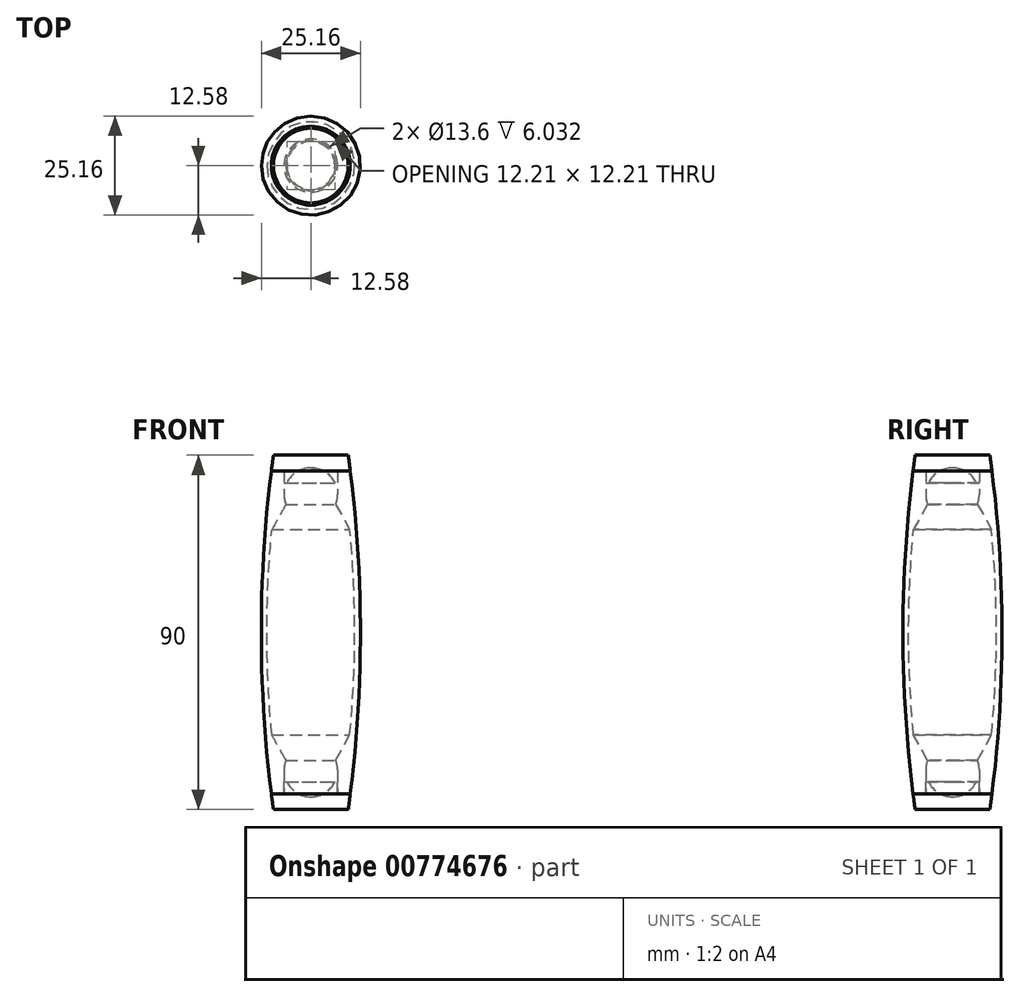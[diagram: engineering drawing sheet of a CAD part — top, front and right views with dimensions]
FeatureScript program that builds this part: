
annotation { "Feature Type Name" : "Feature", "Feature Type Description" : "" }
export const myFeature = defineFeature(function(context is Context, id is Id, definition is map)
    precondition{}
    {
        {
            var Q0;
            Q0=qCreatedBy(makeId("Front.planeOp"),FACE);
            var sketch = newSketch(context, id + "F0", { "sketchPlane" : qUnion([Q0])});
            skPoint(sketch, "E0.middle", {"position": v(0, 0) * mm});
            skLineSegment(sketch, "E1.bottom", {"start": v(0, -45) * mm, "end": v(-12.5, -45) * mm});
            skLineSegment(sketch, "E1.top", {"start": v(0, 45) * mm, "end": v(-12.5, 45) * mm});
            skPoint(sketch, "E2", {"position": v(-9.5, 45) * mm});
            skPoint(sketch, "E3.MirrorP", {"position": v(-9.5, -45) * mm});
            skPoint(sketch, "E4", {"position": v(-12.5, 0) * mm});
            skArc(sketch, "E5", {"start": v(-9.5, 45) * mm, "mid": v(-12.58, 2) * mm, "end": v(-10.02, -41.04) * mm});
            skPoint(sketch, "E6", {"position": v(0, 45) * mm});
            skPoint(sketch, "E7", {"position": v(0, -45) * mm});
            skPoint(sketch, "E1.left.start.orphan", {"position": v(12.5, -45) * mm});
            skPoint(sketch, "E8.orphan", {"position": v(12.5, 45) * mm});
            skPoint(sketch, "E9", {"position": v(0, 41) * mm});
            skLineSegment(sketch, "E10", {"start": v(0, 41.8) * mm, "end": v(0, 45) * mm});
            skLineSegment(sketch, "E11", {"start": v(-8.02, 41.03) * mm, "end": v(-10.02, 41.04) * mm});
            skPoint(sketch, "E12.MirrorP", {"position": v(-8.02, -41.03) * mm});
            skLineSegment(sketch, "E13.MirrorCS", {"start": v(-8.02, -41.03) * mm, "end": v(-10.02, -41.04) * mm});
            skArc(sketch, "E14", {"start": v(0, 41.8) * mm, "mid": v(-3.6, 40.77) * mm, "end": v(-6.1, 38) * mm});
            skLineSegment(sketch, "E15", {"start": v(-8.02, 41.03) * mm, "end": v(-6.8, 41.03) * mm});
            skPoint(sketch, "E16", {"position": v(-6.8, 35) * mm});
            skLineSegment(sketch, "E17", {"start": v(-6.8, 35) * mm, "end": v(-6.8, 41.03) * mm});
            skLineSegment(sketch, "E18", {"start": v(-6.32, 32.5) * mm, "end": v(-9.9, 26.11) * mm});
            skArc(sketch, "E19.trimOffspring", {"start": v(-9.9, 26.11) * mm, "mid": v(-11.16, 0) * mm, "end": v(-9.9, -26.11) * mm});
            skArc(sketch, "E20.trimOffspring", {"start": v(-6.8, 35) * mm, "mid": v(-6.68, 33.73) * mm, "end": v(-6.32, 32.5) * mm});
            skLineSegment(sketch, "E21.trimOffspring", {"start": v(-6.8, 38) * mm, "end": v(-6.1, 38) * mm});
            skPoint(sketch, "E22.orphan", {"position": v(0, -41) * mm});
            skLineSegment(sketch, "E23.MirrorCS", {"start": v(-6.32, -32.5) * mm, "end": v(-9.9, -26.11) * mm});
            skArc(sketch, "E24.MirrorCS", {"start": v(-6.8, -35) * mm, "mid": v(-6.68, -33.73) * mm, "end": v(-6.32, -32.5) * mm});
            skLineSegment(sketch, "E25.MirrorCS", {"start": v(-6.8, -35) * mm, "end": v(-6.8, -41.03) * mm});
            skLineSegment(sketch, "E26.MirrorCS", {"start": v(-8.02, -41.03) * mm, "end": v(-6.8, -41.03) * mm});
            skPoint(sketch, "E27.MirrorCS.end.orphan", {"position": v(-12.5, -45) * mm});
            skSolve(sketch);
        }
        {
            var Q0;
            {var subQ6=sQuery(id+"F0.wireOp",EDGE,"E11");Q0=makeQuery(id+"F0.imprint","IMPRINT",FACE,{"disambiguationData":[TD([[makeQuery(id+"F0.imprint","IMPRINT",EDGE,{"derivedFrom":subQ6}),1.0]])]});}
            var Q1;
            Q1=sQuery(id+"F0.wireOp",EDGE,"E10");
            revolve(context, id + "F1", {"surfaceOperationType" : NewSurfaceOperationType.NEW, "entities" : qUnion([Q0]), "axis" : qUnion([Q1]), "revolveType" : RevolveType.FULL});
        }
        {
            var Q0;
            {var subQ1=sQuery(id+"F0.wireOp",EDGE,"E10");Q0=makeQuery(id+"F0.imprint","IMPRINT",FACE,{"disambiguationData":[TD([[makeQuery(id+"F0.imprint","IMPRINT",EDGE,{"derivedFrom":subQ1}),1.0]])]});}
            var Q1;
            Q1=sQuery(id+"F0.wireOp",EDGE,"E10");
            revolve(context, id + "F2", {"surfaceOperationType" : NewSurfaceOperationType.NEW, "entities" : qUnion([Q0]), "axis" : qUnion([Q1]), "revolveType" : RevolveType.FULL});
        }
        {
            var Q0;
            Q0=makeQuery(id+"F2.opRevolve","SWEPT_BODY",BODY,{"disambiguationData":[OSD([sQuery(id+"F0.wireOp",EDGE,"E1.top"),sQuery(id+"F0.wireOp",EDGE,"E5"),sQuery(id+"F0.wireOp",EDGE,"E10"),sQuery(id+"F0.wireOp",EDGE,"E11"),sQuery(id+"F0.wireOp",EDGE,"E14"),sQuery(id+"F0.wireOp",EDGE,"E15"),sQuery(id+"F0.wireOp",EDGE,"E17"),sQuery(id+"F0.wireOp",EDGE,"E21.trimOffspring")])]});
            var Q1;
            Q1=qCreatedBy(makeId("Top.planeOp"),FACE);
            mirror(context, id + "F3", {"entities" : qUnion([Q0]), "mirrorPlane" : qUnion([Q1])});
        }
    });
